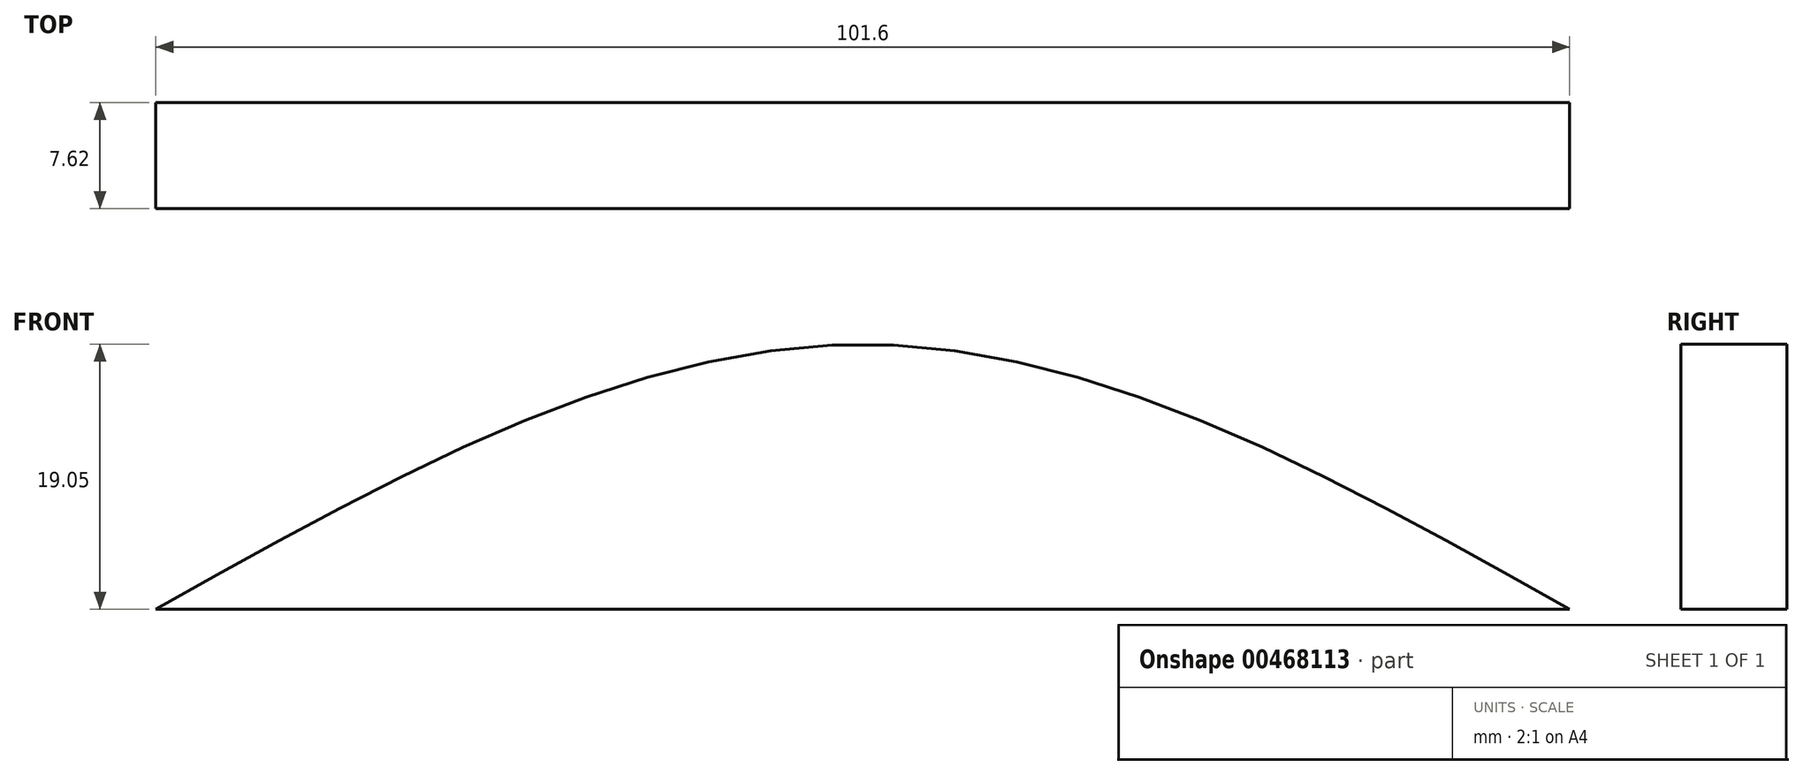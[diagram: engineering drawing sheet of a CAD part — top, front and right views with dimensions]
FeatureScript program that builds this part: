
annotation { "Feature Type Name" : "Feature", "Feature Type Description" : "" }
export const myFeature = defineFeature(function(context is Context, id is Id, definition is map)
    precondition{}
    {
        {
            var Q0;
            Q0=qCreatedBy(makeId("Front.planeOp"),FACE);
            var sketch = newSketch(context, id + "F0", { "sketchPlane" : qUnion([Q0])});
            skLineSegment(sketch, "E0", {"start": v(-50.8, 0) * mm, "end": v(50.8, 0) * mm});
            skLineSegment(sketch, "E1", {"start": v(0, 0) * mm, "end": v(0, 19.05) * mm, "construction": true});
            skFitSpline(sketch, "E2", {"points": [v(-50.8, 0) * mm, v(0, 19.05) * mm, v(50.8, 0) * mm], "startDerivative": vector(101.6, 57.15) * mm, "endDerivative": vector(101.6, -57.15) * mm});
            skSolve(sketch);
        }
        {
            var Q0;
            Q0=makeQuery(id+"F0.imprint","IMPRINT",FACE,{"disambiguationData":[TD([[makeQuery(id+"F0.imprint","IMPRINT",EDGE,{"derivedFrom":sQuery(id+"F0.wireOp",EDGE,"E0")}),1.0]])]});
            extrude(context, id + "F1", {"entities" : qUnion([Q0]), "endBound" : BoundingType.SYMMETRIC, "depth" : 7.62 * mm, "offsetDistance" : 25.4 * mm});
        }
    });
